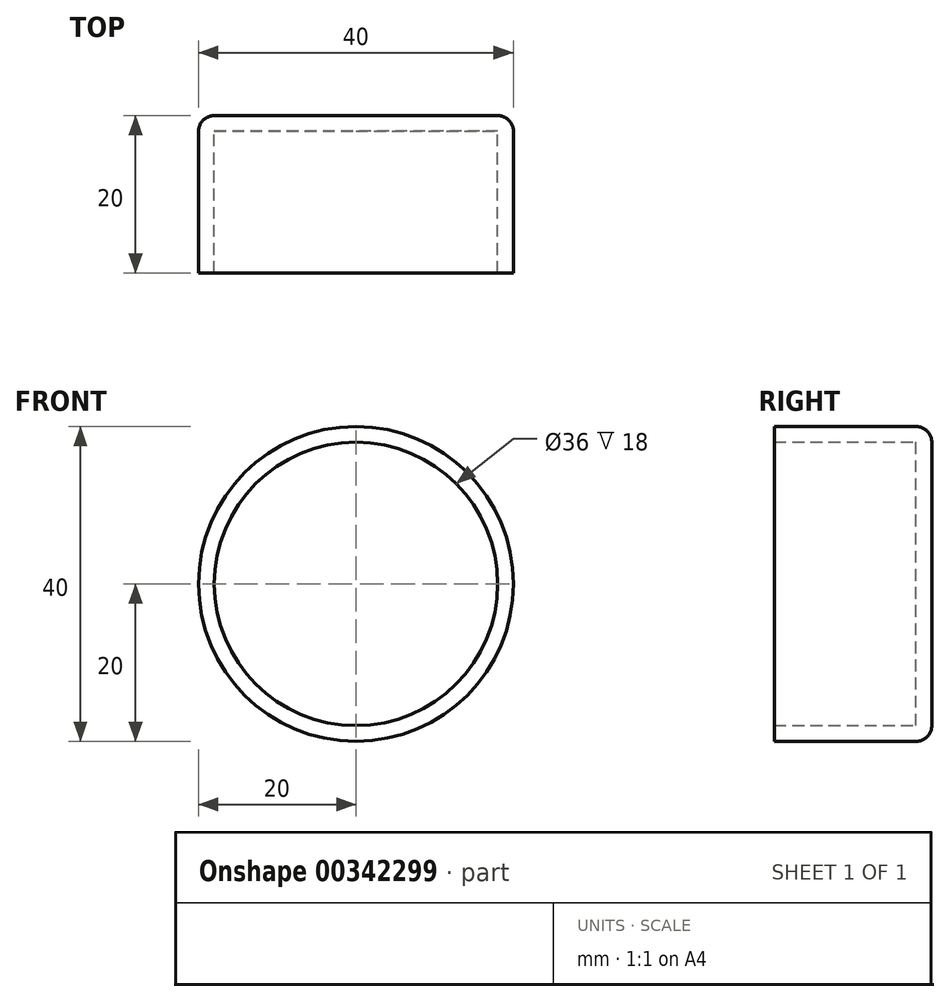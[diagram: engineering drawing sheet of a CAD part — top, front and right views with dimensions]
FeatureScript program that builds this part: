
annotation { "Feature Type Name" : "Feature", "Feature Type Description" : "" }
export const myFeature = defineFeature(function(context is Context, id is Id, definition is map)
    precondition{}
    {
        {
            var Q0;
            Q0=qCreatedBy(makeId("Front.planeOp"),FACE);
            var sketch = newSketch(context, id + "F0", { "sketchPlane" : qUnion([Q0])});
            skCircle(sketch, "E0", {"center": v(0, 0) * mm, "radius": 20 * mm});
            skSolve(sketch);
        }
        {
            var Q0;
            Q0 = qSketchRegion(id + "F0", true);
            extrude(context, id + "F1", {"entities" : qUnion([Q0]), "depth" : 20 * mm});
        }
        {
            var Q0;
            Q0=makeQuery(id+"F1.opExtrude","CAP_FACE",FACE,{"disambiguationData":[OSD([sQuery(id+"F0.wireOp",EDGE,"E0")])],"isStart":false});
            shell(context, id + "F2", {"entities" : qUnion([Q0]), "thickness" : 2 * mm});
        }
        {
            var Q0;
            Q0=makeQuery(id+"F1.opExtrude","CAP_FACE",FACE,{"disambiguationData":[OSD([sQuery(id+"F0.wireOp",EDGE,"E0")])],"isStart":true});
            fillet(context, id + "F3", {"entities" : qUnion([Q0]), "radius" : 2 * mm, "tangentPropagation" : true, "allowEdgeOverflow" : false});
        }
    });
